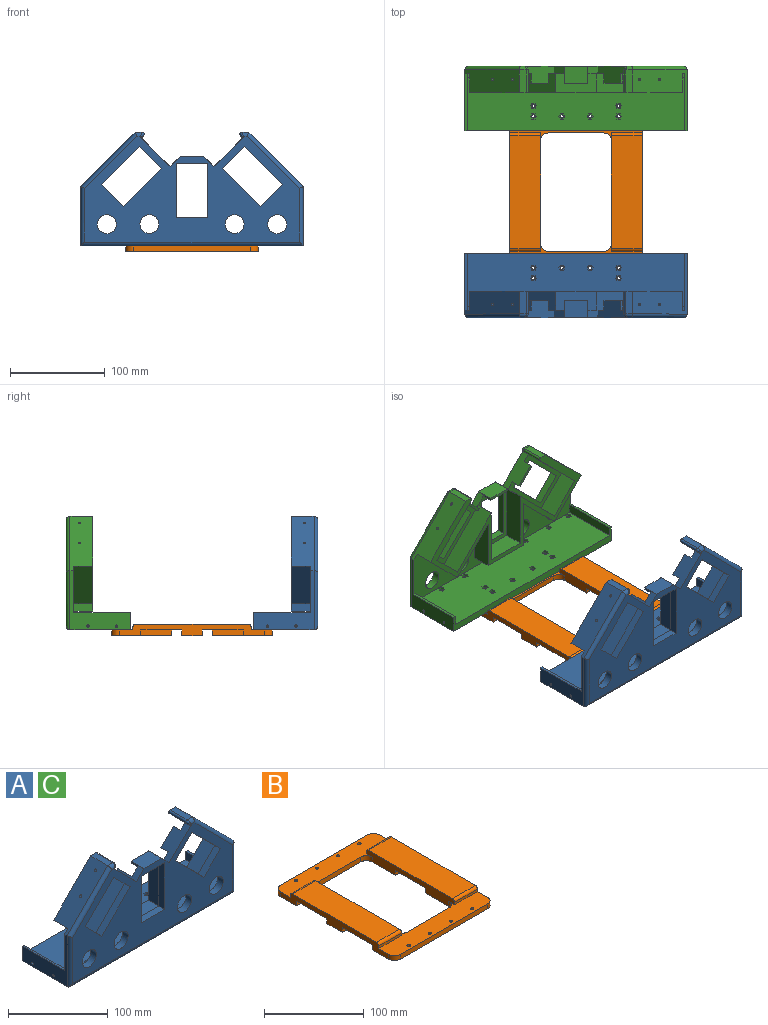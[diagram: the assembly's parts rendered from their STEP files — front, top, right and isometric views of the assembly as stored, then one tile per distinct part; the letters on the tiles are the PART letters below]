
ASSEMBLY  parts=3 mates=6
PART A: 187 faces, bbox 235x68.4x120 mm
  f0: plane 230x60mm, normal (0,0,1), area 13450.4mm2, adj f15,f55,f56,f58,f103,f104,f105,f106
  f1: cylinder r=1.75mm len=5.5mm, axis (0,0,-1), area 60.5mm2, adj f29,f186
  f2: cylinder r=1.75mm len=5.5mm, axis (0,0,-1), area 60.5mm2, adj f29,f179
  f3: cylinder r=1.75mm len=5.5mm, axis (0,0,-1), area 60.5mm2, adj f29,f172
  f4: cylinder r=1.75mm len=5.5mm, axis (0,0,-1), area 60.5mm2, adj f29,f165
  f5: cylinder r=1.75mm len=5.5mm, axis (0,0,-1), area 60.5mm2, adj f29,f158
  f6: cylinder r=1.75mm len=5.5mm, axis (0,0,-1), area 60.5mm2, adj f29,f151
  f7: cylinder r=1.75mm len=5.5mm, axis (0,0,-1), area 60.5mm2, adj f29,f144
  f8: cylinder r=1.75mm len=5.5mm, axis (0,0,-1), area 60.5mm2, adj f29,f137
  f9: cylinder r=1.75mm len=5.5mm, axis (0,0,-1), area 60.5mm2, adj f29,f130
  f10: cylinder r=1.75mm len=5.5mm, axis (0,0,-1), area 60.5mm2, adj f29,f123
  f11: cylinder r=1.75mm len=5.5mm, axis (0,0,-1), area 60.5mm2, adj f29,f116
  f12: cylinder r=1.75mm len=5.5mm, axis (0,0,-1), area 60.5mm2, adj f29,f109
  f13: plane 79.69x79.69mm, normal (0,1,0), area 1047mm2, adj f25,f26,f27,f34,f37,f38,f39,f64
  f14: plane 69.5x43mm, normal (0,1,0), area 962.3mm2, adj f19,f20,f21,f36,f39,f40,f41,f42
  f15: plane 235x65.43mm, normal (0,1,0), area 6953.8mm2, adj f0,f28,f30,f31,f35,f46,f47,f48
  f16: plane 24x7.36mm, normal (0,0,1), area 176.7mm2, adj f35,f53,f78,f100
  f17: plane 227x112mm, normal (0,-1,0), area 13314.3mm2, adj f19,f20,f21,f22,f23,f24,f25,f26
  f18: plane 79.69x79.69mm, normal (0,1,0), area 1047mm2, adj f22,f23,f24,f33,f43,f44,f45,f69
  f19: plane 33x8mm, normal (0,0,-1), area 264mm2, adj f14,f17,f20,f36
  f20: plane 57.2x8mm, normal (-1,0,0), area 457.6mm2, adj f14,f17,f19,f21
  f21: plane 33x8mm, normal (0,0,1), area 264mm2, adj f14,f17,f20,f36
  f22: plane 23.33x23.33mm, normal (-0.71,0,-0.71), area 264mm2, adj f17,f18,f23,f33
  f23: plane 40.45x40.45mm, normal (-0.71,0,0.71), area 457.6mm2, adj f17,f18,f22,f24
  f24: plane 23.33x23.33mm, normal (0.71,0,0.71), area 264mm2, adj f17,f18,f23,f33
  f25: plane 40.45x40.45mm, normal (-0.71,0,-0.71), area 457.6mm2, adj f13,f17,f26,f34
  f26: plane 23.33x23.33mm, normal (-0.71,0,0.71), area 264mm2, adj f13,f17,f25,f27
  f27: plane 40.45x40.45mm, normal (0.71,0,0.71), area 457.6mm2, adj f13,f17,f26,f34
  f28: plane 64x62.5mm, normal (-1,0,0), area 1320.2mm2, adj f15,f29,f35,f57,f58,f80,f94,f96
  f29: plane 235x64mm, normal (0,0,-1), area 14924.5mm2, adj f1,f2,f3,f4,f5,f6,f7,f8
  f30: plane 64x62.5mm, normal (1,0,0), area 1320.2mm2, adj f15,f29,f31,f54,f58,f82,f90,f92
  f31: plane 57.5x57.5mm, normal (0.71,0,0.71), area 1801.9mm2, adj f15,f30,f32,f52,f53,f83,f87,f88
  f32: plane 24x7.36mm, normal (0,0,1), area 176.7mm2, adj f31,f53,f84,f97
  f33: plane 40.45x40.45mm, normal (0.71,0,-0.71), area 457.6mm2, adj f17,f18,f22,f24
  f34: plane 23.33x23.33mm, normal (0.71,0,-0.71), area 264mm2, adj f13,f17,f25,f27
  f35: plane 57.5x57.5mm, normal (-0.71,0,0.71), area 1801.9mm2, adj f15,f16,f28,f46,f53,f79,f85,f86
  f36: plane 57.2x8mm, normal (1,0,0), area 457.6mm2, adj f14,f17,f19,f21
  f37: plane 51.7x51.7mm, normal (-0.71,0,-0.71), area 1471.8mm2, adj f13,f38,f53,f66,f87,f88,f97,f98
  f38: plane 30.41x30.41mm, normal (-0.71,0,0.71), area 860mm2, adj f13,f37,f39,f53
  f39: plane 60.02x60.02mm, normal (0.71,0,0.71), area 1564.4mm2, adj f13,f14,f17,f38,f40,f53,f59,f66
  f40: plane 60.5x20mm, normal (-1,0,0), area 1209.9mm2, adj f14,f39,f41,f53
  f41: plane 43x20mm, normal (0,0,1), area 860mm2, adj f14,f40,f42,f53
  f42: plane 60.5x20mm, normal (1,0,0), area 1209.9mm2, adj f14,f41,f43,f53
  f43: plane 60.02x60.02mm, normal (-0.71,0,0.71), area 1564.4mm2, adj f14,f17,f18,f42,f44,f53,f61,f71
  f44: plane 30.41x30.41mm, normal (0.71,0,0.71), area 860mm2, adj f18,f43,f45,f53
  f45: plane 51.7x51.7mm, normal (0.71,0,-0.71), area 1471.8mm2, adj f18,f44,f53,f71,f85,f86,f100,f101
  f46: plane 40.04x40.04mm, normal (-0.71,0,-0.71), area 1132.4mm2, adj f15,f35,f47,f53
  f47: plane 46.02x46.02mm, normal (0.71,0,-0.71), area 1301.6mm2, adj f15,f46,f48,f53
  f48: plane 53.43x20mm, normal (-1,0,0), area 1068.5mm2, adj f15,f47,f49,f53
  f49: plane 53x20mm, normal (0,0,-1), area 1060mm2, adj f15,f48,f50,f53
  f50: plane 53.43x20mm, normal (1,0,0), area 1068.5mm2, adj f15,f49,f51,f53
  f51: plane 46.02x46.02mm, normal (-0.71,0,-0.71), area 1301.6mm2, adj f15,f50,f52,f53
  f52: plane 40.04x40.04mm, normal (0.71,0,-0.71), area 1132.4mm2, adj f15,f31,f51,f53
  f53: plane 225.11x100mm, normal (0,1,0), area 3296.6mm2, adj f16,f31,f32,f35,f37,f38,f39,f40
  f54: plane 60x2.5mm, normal (0,0,1), area 150mm2, adj f15,f30,f55,f58
  f55: plane 60x10mm, normal (-1,0,0), area 600mm2, adj f0,f15,f54,f58
  f56: plane 60x10mm, normal (1,0,0), area 600mm2, adj f0,f15,f57,f58
  f57: plane 60x2.5mm, normal (0,0,1), area 150mm2, adj f15,f28,f56,f58
  f58: plane 235x18mm, normal (0,1,0), area 1930mm2, adj f0,f28,f29,f30,f54,f55,f56,f57
  f59: plane 18x2.5mm, normal (1,0,0), area 26.6mm2, adj f14,f17,f39,f60,f62,f63
  f60: plane 25x18mm, normal (0,0,1), area 450mm2, adj f17,f59,f61,f63
  f61: plane 18x2.5mm, normal (-1,0,0), area 26.6mm2, adj f14,f17,f43,f60,f62,f63
  f62: plane 25x10mm, normal (0,0,-1), area 250mm2, adj f14,f59,f61,f63
  f63: plane 25x2.5mm, normal (0,1,0), area 62.5mm2, adj f59,f60,f61,f62
  f64: plane 17.68x17.68mm, normal (0.71,0,-0.71), area 250mm2, adj f13,f65,f67,f68
  f65: plane 10x1.77mm, normal (0.71,0,0.71), area 25mm2, adj f13,f64,f66,f68
  f66: plane 31.82x31.82mm, normal (-0.71,0,0.71), area 594.9mm2, adj f13,f17,f37,f39,f65,f67,f68,f99
  f67: plane 10x1.77mm, normal (-0.71,0,-0.71), area 25mm2, adj f13,f64,f66,f68
  f68: plane 19.45x19.45mm, normal (0,1,0), area 62.5mm2, adj f64,f65,f66,f67
  f69: plane 17.68x17.68mm, normal (-0.71,0,-0.71), area 250mm2, adj f18,f70,f72,f73
  f70: plane 10x1.77mm, normal (0.71,0,-0.71), area 25mm2, adj f18,f69,f71,f73
  f71: plane 31.82x31.82mm, normal (0.71,0,0.71), area 594.9mm2, adj f17,f18,f43,f45,f70,f72,f73,f102
  f72: plane 10x1.77mm, normal (-0.71,0,0.71), area 25mm2, adj f18,f69,f71,f73
  f73: plane 19.45x19.45mm, normal (0,1,0), area 62.5mm2, adj f69,f70,f71,f72
  f74: cylinder r=10mm len=20mm, axis (0,1,0), area 502.7mm2, adj f15,f17
  f75: cylinder r=10mm len=20mm, axis (0,1,0), area 502.7mm2, adj f15,f17
  f76: cylinder r=10mm len=20mm, axis (0,1,0), area 502.7mm2, adj f15,f17
  f77: cylinder r=10mm len=20mm, axis (0,1,0), area 502.7mm2, adj f15,f17
  f78: cylinder r=4mm len=7.36mm, axis (1,0,0), area 37.9mm2, adj f16,f17,f79,f101
  f79: cylinder r=4mm len=60.33mm, axis (0.71,0,0.71), area 503.4mm2, adj f17,f35,f78,f80
  f80: cylinder r=4mm len=62.5mm, axis (0,0,1), area 379.8mm2, adj f17,f28,f79,f81
  f81: cylinder r=4mm len=235mm, axis (-1,0,0), area 1458.3mm2, adj f17,f29,f80,f82
  f82: cylinder r=4mm len=62.5mm, axis (0,0,-1), area 379.8mm2, adj f17,f30,f81,f83
  f83: cylinder r=4mm len=60.33mm, axis (0.71,0,-0.71), area 503.4mm2, adj f17,f31,f82,f84
  f84: cylinder r=4mm len=7.36mm, axis (1,0,0), area 37.9mm2, adj f17,f32,f83,f98
  f85: cylinder r=1.25mm len=7.86mm, axis (-0.71,0,0.71), area 67.7mm2, adj f35,f45
  f86: cylinder r=1.25mm len=7.86mm, axis (-0.71,0,0.71), area 67.7mm2, adj f35,f45
  f87: cylinder r=1.25mm len=7.86mm, axis (0.71,0,0.71), area 67.7mm2, adj f31,f37
  f88: cylinder r=1.25mm len=7.86mm, axis (0.71,0,0.71), area 67.7mm2, adj f31,f37
  f89: cone r=0mm half-angle=59deg, axis (1,0,0), area 5.7mm2, adj f90
  f90: cylinder r=1.25mm len=20mm, axis (1,0,0), area 157.1mm2, adj f30,f89
  f91: cone r=0mm half-angle=59deg, axis (1,0,0), area 5.7mm2, adj f92
  f92: cylinder r=1.25mm len=20mm, axis (1,0,0), area 157.1mm2, adj f30,f91
  f93: cone r=0mm half-angle=59deg, axis (-1,0,0), area 5.7mm2, adj f94
  f94: cylinder r=1.25mm len=20mm, axis (-1,0,0), area 157.1mm2, adj f28,f93
  f95: cone r=0mm half-angle=59deg, axis (-1,0,0), area 5.7mm2, adj f96
  f96: cylinder r=1.25mm len=20mm, axis (-1,0,0), area 157.1mm2, adj f28,f95
  f97: cylinder r=2mm len=24mm, axis (0,-1,0), area 113.1mm2, adj f32,f37,f53,f98
  f98: bspline ~7.18x5.92mm, area 24.9mm2, adj f37,f84,f97,f99
  f99: cylinder r=2mm len=2mm, axis (0.71,0,-0.71), area 1.8mm2, adj f17,f37,f66,f98
  f100: cylinder r=2mm len=24mm, axis (0,1,0), area 113.1mm2, adj f16,f45,f53,f101
  f101: bspline ~7.18x5.92mm, area 24.9mm2, adj f45,f78,f100,f102
  f102: cylinder r=2mm len=2mm, axis (0.71,0,0.71), area 1.8mm2, adj f17,f45,f71,f101
  f103: plane 2.9x2.5mm, normal (-0.87,0.5,0), area 8.4mm2, adj f0,f104,f108,f109
  f104: plane 2.9x2.5mm, normal (-0.87,-0.5,0), area 8.4mm2, adj f0,f103,f105,f109
  f105: plane 3.35x2.5mm, normal (0,-1,0), area 8.4mm2, adj f0,f104,f106,f109
  f106: plane 2.9x2.5mm, normal (0.87,-0.5,0), area 8.4mm2, adj f0,f105,f107,f109
  f107: plane 2.9x2.5mm, normal (0.87,0.5,0), area 8.4mm2, adj f0,f106,f108,f109
  f108: plane 3.35x2.5mm, normal (0,1,0), area 8.4mm2, adj f0,f103,f107,f109
  f109: plane 6.7x5.8mm, normal (0,0,1), area 19.5mm2, adj f12,f103,f104,f105,f106,f107,f108
  f110: plane 2.9x2.5mm, normal (0.87,-0.5,0), area 8.4mm2, adj f0,f111,f115,f116
  f111: plane 2.9x2.5mm, normal (0.87,0.5,0), area 8.4mm2, adj f0,f110,f112,f116
  f112: plane 3.35x2.5mm, normal (0,1,0), area 8.4mm2, adj f0,f111,f113,f116
  f113: plane 2.9x2.5mm, normal (-0.87,0.5,0), area 8.4mm2, adj f0,f112,f114,f116
  f114: plane 2.9x2.5mm, normal (-0.87,-0.5,0), area 8.4mm2, adj f0,f113,f115,f116
  f115: plane 3.35x2.5mm, normal (0,-1,0), area 8.4mm2, adj f0,f110,f114,f116
  f116: plane 6.7x5.8mm, normal (0,0,1), area 19.5mm2, adj f11,f110,f111,f112,f113,f114,f115
  f117: plane 2.9x2.5mm, normal (0.87,0.5,0), area 8.4mm2, adj f0,f118,f122,f123
  f118: plane 3.35x2.5mm, normal (0,1,0), area 8.4mm2, adj f0,f117,f119,f123
  f119: plane 2.9x2.5mm, normal (-0.87,0.5,0), area 8.4mm2, adj f0,f118,f120,f123
  f120: plane 2.9x2.5mm, normal (-0.87,-0.5,0), area 8.4mm2, adj f0,f119,f121,f123
  f121: plane 3.35x2.5mm, normal (0,-1,0), area 8.4mm2, adj f0,f120,f122,f123
  f122: plane 2.9x2.5mm, normal (0.87,-0.5,0), area 8.4mm2, adj f0,f117,f121,f123
  f123: plane 6.7x5.8mm, normal (0,0,1), area 19.5mm2, adj f10,f117,f118,f119,f120,f121,f122
  f124: plane 2.9x2.5mm, normal (-0.87,0.5,0), area 8.4mm2, adj f0,f125,f129,f130
  f125: plane 2.9x2.5mm, normal (-0.87,-0.5,0), area 8.4mm2, adj f0,f124,f126,f130
  f126: plane 3.35x2.5mm, normal (0,-1,0), area 8.4mm2, adj f0,f125,f127,f130
  f127: plane 2.9x2.5mm, normal (0.87,-0.5,0), area 8.4mm2, adj f0,f126,f128,f130
  f128: plane 2.9x2.5mm, normal (0.87,0.5,0), area 8.4mm2, adj f0,f127,f129,f130
  f129: plane 3.35x2.5mm, normal (0,1,0), area 8.4mm2, adj f0,f124,f128,f130
  f130: plane 6.7x5.8mm, normal (0,0,1), area 19.5mm2, adj f9,f124,f125,f126,f127,f128,f129
  f131: plane 3.35x2.5mm, normal (0,-1,0), area 8.4mm2, adj f0,f132,f136,f137
  f132: plane 2.9x2.5mm, normal (0.87,-0.5,0), area 8.4mm2, adj f0,f131,f133,f137
  f133: plane 2.9x2.5mm, normal (0.87,0.5,0), area 8.4mm2, adj f0,f132,f134,f137
  f134: plane 3.35x2.5mm, normal (0,1,0), area 8.4mm2, adj f0,f133,f135,f137
  f135: plane 2.9x2.5mm, normal (-0.87,0.5,0), area 8.4mm2, adj f0,f134,f136,f137
  f136: plane 2.9x2.5mm, normal (-0.87,-0.5,0), area 8.4mm2, adj f0,f131,f135,f137
  f137: plane 6.7x5.8mm, normal (0,0,1), area 19.5mm2, adj f8,f131,f132,f133,f134,f135,f136
  f138: plane 2.9x2.5mm, normal (0.87,-0.5,0), area 8.4mm2, adj f0,f139,f143,f144
  f139: plane 2.9x2.5mm, normal (0.87,0.5,0), area 8.4mm2, adj f0,f138,f140,f144
  f140: plane 3.35x2.5mm, normal (0,1,0), area 8.4mm2, adj f0,f139,f141,f144
  f141: plane 2.9x2.5mm, normal (-0.87,0.5,0), area 8.4mm2, adj f0,f140,f142,f144
  f142: plane 2.9x2.5mm, normal (-0.87,-0.5,0), area 8.4mm2, adj f0,f141,f143,f144
  f143: plane 3.35x2.5mm, normal (0,-1,0), area 8.4mm2, adj f0,f138,f142,f144
  f144: plane 6.7x5.8mm, normal (0,0,1), area 19.5mm2, adj f7,f138,f139,f140,f141,f142,f143
  f145: plane 3.35x2.5mm, normal (0,1,0), area 8.4mm2, adj f0,f146,f150,f151
  f146: plane 2.9x2.5mm, normal (-0.87,0.5,0), area 8.4mm2, adj f0,f145,f147,f151
  f147: plane 2.9x2.5mm, normal (-0.87,-0.5,0), area 8.4mm2, adj f0,f146,f148,f151
  f148: plane 3.35x2.5mm, normal (0,-1,0), area 8.4mm2, adj f0,f147,f149,f151
  f149: plane 2.9x2.5mm, normal (0.87,-0.5,0), area 8.4mm2, adj f0,f148,f150,f151
  f150: plane 2.9x2.5mm, normal (0.87,0.5,0), area 8.4mm2, adj f0,f145,f149,f151
  f151: plane 6.7x5.8mm, normal (0,0,1), area 19.5mm2, adj f6,f145,f146,f147,f148,f149,f150
  f152: plane 2.9x2.5mm, normal (-0.87,0.5,0), area 8.4mm2, adj f0,f153,f157,f158
  f153: plane 2.9x2.5mm, normal (-0.87,-0.5,0), area 8.4mm2, adj f0,f152,f154,f158
  f154: plane 3.35x2.5mm, normal (0,-1,0), area 8.4mm2, adj f0,f153,f155,f158
  f155: plane 2.9x2.5mm, normal (0.87,-0.5,0), area 8.4mm2, adj f0,f154,f156,f158
  f156: plane 2.9x2.5mm, normal (0.87,0.5,0), area 8.4mm2, adj f0,f155,f157,f158
  f157: plane 3.35x2.5mm, normal (0,1,0), area 8.4mm2, adj f0,f152,f156,f158
  f158: plane 6.7x5.8mm, normal (0,0,1), area 19.5mm2, adj f5,f152,f153,f154,f155,f156,f157
  f159: plane 3.35x2.5mm, normal (0,1,0), area 8.4mm2, adj f0,f160,f164,f165
  f160: plane 2.9x2.5mm, normal (-0.87,0.5,0), area 8.4mm2, adj f0,f159,f161,f165
  f161: plane 2.9x2.5mm, normal (-0.87,-0.5,0), area 8.4mm2, adj f0,f160,f162,f165
  f162: plane 3.35x2.5mm, normal (0,-1,0), area 8.4mm2, adj f0,f161,f163,f165
  f163: plane 2.9x2.5mm, normal (0.87,-0.5,0), area 8.4mm2, adj f0,f162,f164,f165
  f164: plane 2.9x2.5mm, normal (0.87,0.5,0), area 8.4mm2, adj f0,f159,f163,f165
  f165: plane 6.7x5.8mm, normal (0,0,1), area 19.5mm2, adj f4,f159,f160,f161,f162,f163,f164
  f166: plane 3.35x2.5mm, normal (0,1,0), area 8.4mm2, adj f0,f167,f171,f172
  f167: plane 2.9x2.5mm, normal (-0.87,0.5,0), area 8.4mm2, adj f0,f166,f168,f172
  f168: plane 2.9x2.5mm, normal (-0.87,-0.5,0), area 8.4mm2, adj f0,f167,f169,f172
  f169: plane 3.35x2.5mm, normal (0,-1,0), area 8.4mm2, adj f0,f168,f170,f172
  f170: plane 2.9x2.5mm, normal (0.87,-0.5,0), area 8.4mm2, adj f0,f169,f171,f172
  f171: plane 2.9x2.5mm, normal (0.87,0.5,0), area 8.4mm2, adj f0,f166,f170,f172
  f172: plane 6.7x5.8mm, normal (0,0,1), area 19.5mm2, adj f3,f166,f167,f168,f169,f170,f171
  f173: plane 2.9x2.5mm, normal (0.87,-0.5,0), area 8.4mm2, adj f0,f174,f178,f179
  f174: plane 2.9x2.5mm, normal (0.87,0.5,0), area 8.4mm2, adj f0,f173,f175,f179
  f175: plane 3.35x2.5mm, normal (0,1,0), area 8.4mm2, adj f0,f174,f176,f179
  f176: plane 2.9x2.5mm, normal (-0.87,0.5,0), area 8.4mm2, adj f0,f175,f177,f179
  f177: plane 2.9x2.5mm, normal (-0.87,-0.5,0), area 8.4mm2, adj f0,f176,f178,f179
  f178: plane 3.35x2.5mm, normal (0,-1,0), area 8.4mm2, adj f0,f173,f177,f179
  f179: plane 6.7x5.8mm, normal (0,0,1), area 19.5mm2, adj f2,f173,f174,f175,f176,f177,f178
  f180: plane 3.35x2.5mm, normal (0,-1,0), area 8.4mm2, adj f0,f181,f185,f186
  f181: plane 2.9x2.5mm, normal (0.87,-0.5,0), area 8.4mm2, adj f0,f180,f182,f186
  f182: plane 2.9x2.5mm, normal (0.87,0.5,0), area 8.4mm2, adj f0,f181,f183,f186
  f183: plane 3.35x2.5mm, normal (0,1,0), area 8.4mm2, adj f0,f182,f184,f186
  f184: plane 2.9x2.5mm, normal (-0.87,0.5,0), area 8.4mm2, adj f0,f183,f185,f186
  f185: plane 2.9x2.5mm, normal (-0.87,-0.5,0), area 8.4mm2, adj f0,f180,f184,f186
  f186: plane 6.7x5.8mm, normal (0,0,1), area 19.5mm2, adj f1,f180,f181,f182,f183,f184,f185
PART B: 64 faces, bbox 140x170x12 mm
  f0: plane 140x63.5mm, normal (0,0,-1), area 4626mm2, adj f3,f4,f9,f10,f15,f30,f33,f36
  f1: plane 32.5x22mm, normal (0,0,-1), area 715mm2, adj f10,f42,f43,f46
  f2: plane 140x63.5mm, normal (0,0,-1), area 4626mm2, adj f3,f4,f10,f11,f18,f21,f24,f27
  f3: plane 154x12mm, normal (1,0,0), area 1412.1mm2, adj f0,f2,f8,f12,f37,f38,f39,f49
  f4: plane 125x12mm, normal (-1,0,0), area 1142.1mm2, adj f0,f2,f8,f12,f37,f38,f39,f49
  f5: plane 32.5x3mm, normal (0,1,0), area 97.5mm2, adj f8,f10,f42,f63
  f6: plane 32.5x3mm, normal (0,-1,0), area 97.5mm2, adj f10,f12,f42,f62
  f7: plane 119x32.5mm, normal (0,0,1), area 3867.5mm2, adj f10,f42,f62,f63
  f8: plane 140x30.5mm, normal (0,0,1), area 3111.5mm2, adj f3,f4,f5,f9,f10,f13,f28,f31
  f9: plane 124x6mm, normal (0,1,0), area 744mm2, adj f0,f8,f56,f59
  f10: plane 154x12mm, normal (-1,0,0), area 1154.1mm2, adj f0,f1,f2,f5,f6,f7,f8,f12
  f11: plane 124x6mm, normal (0,-1,0), area 744mm2, adj f2,f12,f57,f58
  f12: plane 140x30.5mm, normal (0,0,1), area 3111.5mm2, adj f3,f4,f6,f10,f11,f16,f19,f22
  f13: cylinder r=1.75mm len=3.5mm, axis (0,0,-1), area 22mm2, adj f8,f14
  f14: plane 6.5x6.5mm, normal (0,0,-1), area 23.6mm2, adj f13,f15
  f15: cylinder r=3.25mm len=6.5mm, axis (0,0,-1), area 81.7mm2, adj f0,f14
  f16: cylinder r=1.75mm len=3.5mm, axis (0,0,-1), area 22mm2, adj f12,f17
  f17: plane 6.5x6.5mm, normal (0,0,-1), area 23.6mm2, adj f16,f18
  f18: cylinder r=3.25mm len=6.5mm, axis (0,0,-1), area 81.7mm2, adj f2,f17
  f19: cylinder r=1.75mm len=3.5mm, axis (0,0,-1), area 22mm2, adj f12,f20
  f20: plane 6.5x6.5mm, normal (0,0,-1), area 23.6mm2, adj f19,f21
  f21: cylinder r=3.25mm len=6.5mm, axis (0,0,-1), area 81.7mm2, adj f2,f20
  f22: cylinder r=1.75mm len=3.5mm, axis (0,0,-1), area 22mm2, adj f12,f23
  f23: plane 6.5x6.5mm, normal (0,0,-1), area 23.6mm2, adj f22,f24
  f24: cylinder r=3.25mm len=6.5mm, axis (0,0,-1), area 81.7mm2, adj f2,f23
  f25: cylinder r=1.75mm len=3.5mm, axis (0,0,-1), area 22mm2, adj f12,f26
  f26: plane 6.5x6.5mm, normal (0,0,-1), area 23.6mm2, adj f25,f27
  f27: cylinder r=3.25mm len=6.5mm, axis (0,0,-1), area 81.7mm2, adj f2,f26
  f28: cylinder r=1.75mm len=3.5mm, axis (0,0,-1), area 22mm2, adj f8,f29
  f29: plane 6.5x6.5mm, normal (0,0,-1), area 23.6mm2, adj f28,f30
  f30: cylinder r=3.25mm len=6.5mm, axis (0,0,-1), area 81.7mm2, adj f0,f29
  f31: cylinder r=1.75mm len=3.5mm, axis (0,0,-1), area 22mm2, adj f8,f32
  f32: plane 6.5x6.5mm, normal (0,0,-1), area 23.6mm2, adj f31,f33
  f33: cylinder r=3.25mm len=6.5mm, axis (0,0,-1), area 81.7mm2, adj f0,f32
  f34: cylinder r=1.75mm len=3.5mm, axis (0,0,-1), area 22mm2, adj f8,f35
  f35: plane 6.5x6.5mm, normal (0,0,-1), area 23.6mm2, adj f34,f36
  f36: cylinder r=3.25mm len=6.5mm, axis (0,0,-1), area 81.7mm2, adj f0,f35
  f37: plane 32.5x3mm, normal (0,1,0), area 97.5mm2, adj f3,f4,f8,f61
  f38: plane 32.5x3mm, normal (0,-1,0), area 97.5mm2, adj f3,f4,f12,f60
  f39: plane 119x32.5mm, normal (0,0,1), area 3867.5mm2, adj f3,f4,f60,f61
  f40: plane 59x6mm, normal (0,-1,0), area 354mm2, adj f0,f8,f52,f53
  f41: plane 59x6mm, normal (0,1,0), area 354mm2, adj f2,f12,f54,f55
  f42: plane 125x12mm, normal (1,0,0), area 884.1mm2, adj f0,f1,f2,f5,f6,f7,f8,f12
  f43: plane 32.5x6mm, normal (0,-1,0), area 195mm2, adj f1,f10,f42,f45
  f44: plane 32.5x6mm, normal (0,1,0), area 195mm2, adj f2,f10,f42,f45
  f45: plane 43x32.5mm, normal (0,0,-1), area 1397.5mm2, adj f10,f42,f43,f44
  f46: plane 32.5x6mm, normal (0,1,0), area 195mm2, adj f1,f10,f42,f48
  f47: plane 32.5x6mm, normal (0,-1,0), area 195mm2, adj f0,f10,f42,f48
  f48: plane 43x32.5mm, normal (0,0,-1), area 1397.5mm2, adj f10,f42,f46,f47
  f49: plane 32.5x6mm, normal (0,1,0), area 195mm2, adj f2,f3,f4,f51
  f50: plane 32.5x6mm, normal (0,-1,0), area 195mm2, adj f0,f3,f4,f51
  f51: plane 43x32.5mm, normal (0,0,-1), area 1397.5mm2, adj f3,f4,f49,f50
  f52: cylinder r=8mm len=8mm, axis (0,0,-1), area 75.4mm2, adj f0,f4,f8,f40
  f53: cylinder r=8mm len=8mm, axis (0,0,1), area 75.4mm2, adj f0,f8,f40,f42
  f54: cylinder r=8mm len=8mm, axis (0,0,1), area 75.4mm2, adj f2,f4,f12,f41
  f55: cylinder r=8mm len=8mm, axis (0,0,-1), area 75.4mm2, adj f2,f12,f41,f42
  f56: cylinder r=8mm len=8mm, axis (0,0,1), area 75.4mm2, adj f0,f8,f9,f10
  f57: cylinder r=8mm len=8mm, axis (0,0,-1), area 75.4mm2, adj f2,f10,f11,f12
  f58: cylinder r=8mm len=8mm, axis (0,0,1), area 75.4mm2, adj f2,f3,f11,f12
  f59: cylinder r=8mm len=8mm, axis (0,0,-1), area 75.4mm2, adj f0,f3,f8,f9
  f60: cylinder r=3mm len=32.5mm, axis (-1,0,0), area 153.2mm2, adj f3,f4,f38,f39
  f61: cylinder r=3mm len=32.5mm, axis (1,0,0), area 153.2mm2, adj f3,f4,f37,f39
  f62: cylinder r=3mm len=32.5mm, axis (-1,0,0), area 153.2mm2, adj f6,f7,f10,f42
  f63: cylinder r=3mm len=32.5mm, axis (1,0,0), area 153.2mm2, adj f5,f7,f10,f42
PART C: same geometry as A
PLACE A t=(209.86,-87.61,-63.49)mm
PLACE B t=(209.86,37.39,-69.49)mm
PLACE C rot(axis=(0,0,-1),180deg) t=(209.86,162.39,-63.49)mm
MATE cylindrical C.f11 <-> B.f34  axis (0,0,-1) through (129.86,158.39,-63.49)mm
MATE planar B.f12 <-> A.f29  axis (0,0,1) through (209.86,-36.09,-63.49)mm
MATE cylindrical B.f22 <-> A.f11  axis (0,0,-1) through (194.86,-42.61,-69.49)mm
MATE cylindrical C.f4 <-> B.f31  axis (0,0,-1) through (164.86,128.39,-63.49)mm
MATE cylindrical B.f19 <-> A.f4  axis (0,0,-1) through (224.86,-42.61,-69.49)mm
MATE planar C.f29 <-> B.f8  axis (0,0,-1) through (209.86,134.34,-63.49)mm
